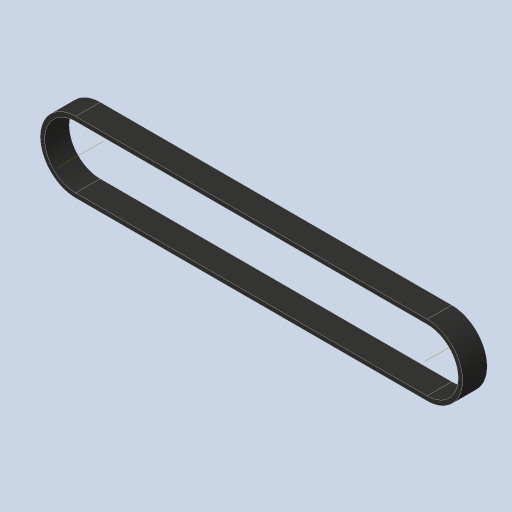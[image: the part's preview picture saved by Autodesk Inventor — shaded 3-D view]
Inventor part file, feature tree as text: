
AUTODESK INVENTOR PART (.ipt)
format: ipt  version: 2023.4 (Build 274418000, 418)  size: 165,376 bytes
history: native  units: in
note: dims shown in document units (in); Inventor stores cm internally (conversion verified against a paired STEP export)
features: sketch x3, extrude x1, other x1, projected_geometry x1
ambient origin geometry x8: Origin, YZ Plane, XZ Plane, XY Plane, X Axis, Y Axis, Z Axis, Center Point
bodies: Body1 (feature_tree)
feature tree (6):
  sketch  "Sketch2"  dims[d0=0.9023in d1=0.9023in]
  extrude  "Extrusion2"  Depth=0.9023in
  sketch  "Sketch5"  dims[d3=1.4174in d5=4.7834in d9=0.0787in d10=0.0598in d11=0.0299in d12=0.0219in d13=0.0219in d14=0.0059in d15=0.0059in d20=0.3346in d21=0.0in d22=0.0787in d23=0.0598in d24=0.0299in d25=0.0219in d26=0.0219in d27=0.0059in d28=0.0059in d29=0.0299in d30=0.0394in d31=0.0787in d32=0.0232in d34=0.0219in d35=0.0in d36=0.0in d37=0.0059in d38=0.0022in d39=0.0022in d40=0.0in d41=0.0in d42=0.0081in d43=0.0081in d44=0.0299in]
  other  "Work Axis1"
  sketch  "Sketch4"  dims[d2=1.4174in]
  projected_geometry  "Projected Loop1"
